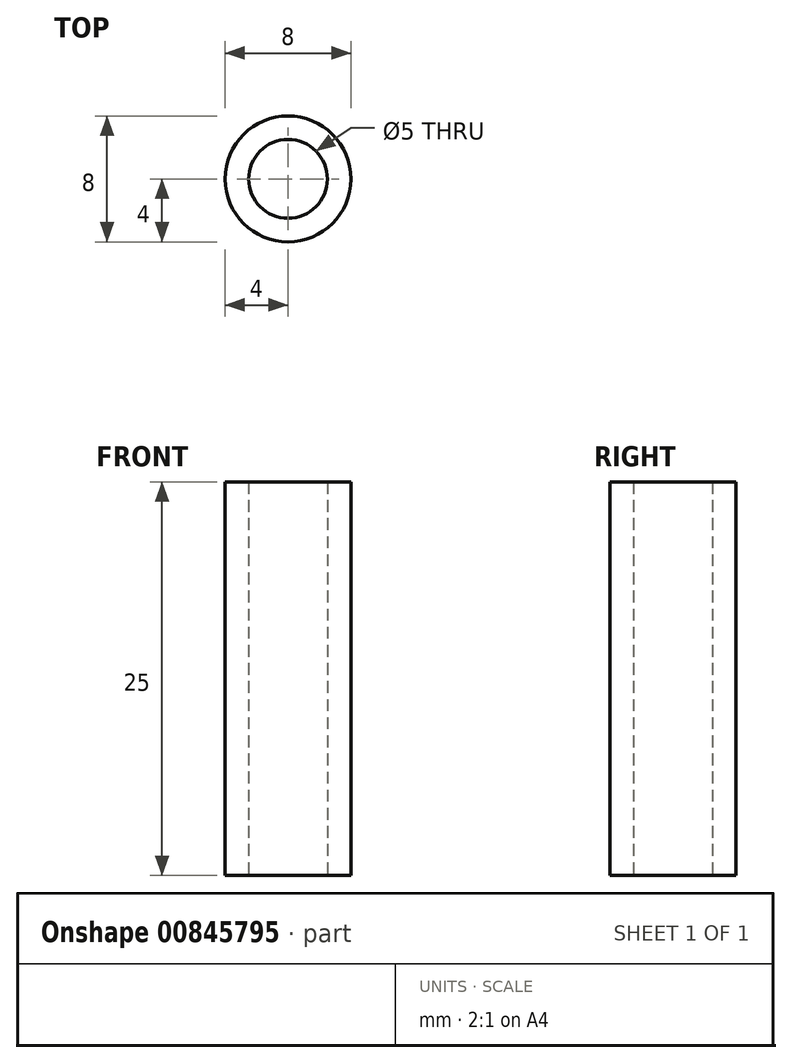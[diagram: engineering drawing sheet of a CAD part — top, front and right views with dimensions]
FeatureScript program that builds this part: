
annotation { "Feature Type Name" : "Feature", "Feature Type Description" : "" }
export const myFeature = defineFeature(function(context is Context, id is Id, definition is map)
    precondition{}
    {
        {
            var Q0;
            Q0=qCreatedBy(makeId("Top.planeOp"),FACE);
            var sketch = newSketch(context, id + "F0", { "sketchPlane" : qUnion([Q0])});
            skCircle(sketch, "E0", {"center": v(0, 0) * mm, "radius": 4 * mm});
            skCircle(sketch, "E1", {"center": v(0, 0) * mm, "radius": 2.5 * mm});
            skSolve(sketch);
        }
        {
            var Q0;
            Q0=makeQuery(id+"F0.imprint","IMPRINT",FACE,{"disambiguationData":[TD([[makeQuery(id+"F0.imprint","IMPRINT",EDGE,{"derivedFrom":sQuery(id+"F0.wireOp",EDGE,"E0")}),1.0]])]});
            extrude(context, id + "F1", {"entities" : qUnion([Q0]), "depth" : 25 * mm, "offsetDistance" : 25 * mm});
        }
    });
